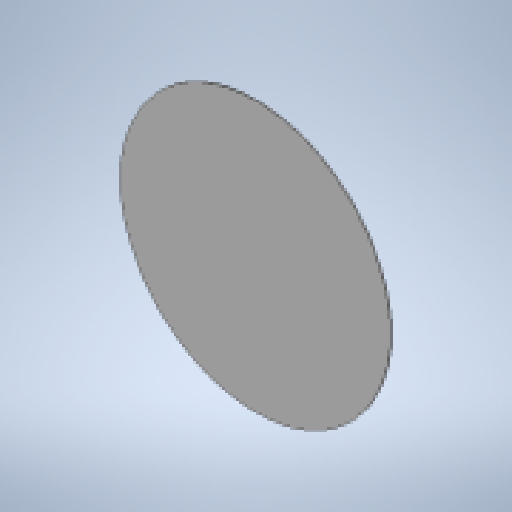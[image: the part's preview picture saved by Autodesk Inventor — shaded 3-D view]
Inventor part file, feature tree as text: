
AUTODESK INVENTOR PART (.ipt)
format: ipt  version: 2025 (Build 290162010, 162A)  size: 165,376 bytes
history: native  units: mm
features: sketch x2, sheet_metal_op x1, other x1
ambient origin geometry x8: Origin, YZ Plane, XZ Plane, XY Plane, X Axis, Y Axis, Z Axis, Center Point
bodies: Solid1 (feature_tree)
feature tree (4):
  sheet_metal_op  "Face1"
  sketch  "Sketch1"  dims[d15=2.0mm]
  other  "Plate1"
  sketch  "Sketch Circular Pattern1"  dims[d31=28.0mm d32=110.0mm d39=80.0mm d40=8.0mm d41=80.0mm d43=360.0deg]
